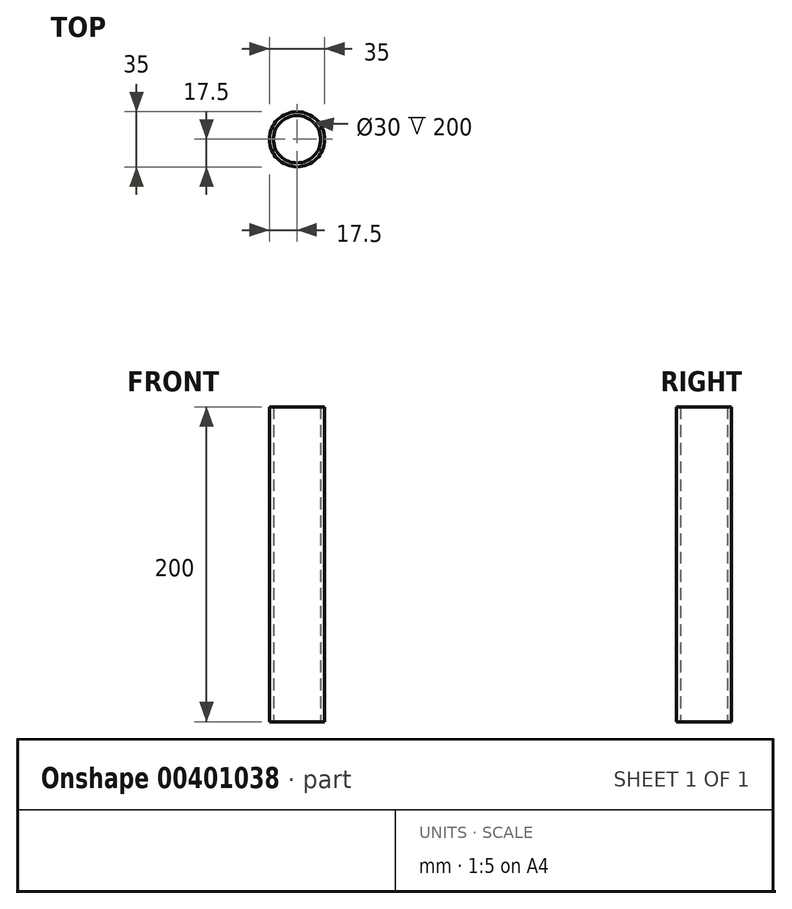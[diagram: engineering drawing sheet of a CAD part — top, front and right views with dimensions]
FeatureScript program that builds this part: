
annotation { "Feature Type Name" : "Feature", "Feature Type Description" : "" }
export const myFeature = defineFeature(function(context is Context, id is Id, definition is map)
    precondition{}
    {
        {
            var Q0;
            Q0=qCreatedBy(makeId("Top.planeOp"),FACE);
            var sketch = newSketch(context, id + "F0", { "sketchPlane" : qUnion([Q0])});
            skCircle(sketch, "E0", {"center": v(0, 0) * mm, "radius": 15 * mm});
            skCircle(sketch, "E1", {"center": v(0, 0) * mm, "radius": 17.5 * mm});
            skSolve(sketch);
        }
        {
            var Q0;
            Q0=makeQuery(id+"F0.imprint","IMPRINT",FACE,{"disambiguationData":[TD([[makeQuery(id+"F0.imprint","IMPRINT",EDGE,{"derivedFrom":sQuery(id+"F0.wireOp",EDGE,"E0")}),-1.0]])]});
            extrude(context, id + "F1", {"entities" : qUnion([Q0]), "depth" : 200 * mm});
        }
    });
